# Revit family: Rough_In_Valve-American_Standard-R950-SS
name_source: partatom
category: Plumbing Fixtures
revit_build: Autodesk Revit 2014 (Build: 20130308_1515(x64)
units: mm (PartAtom-declared; Revit-internal decimal feet)

## types (2) — shared parameters
Assembly Code = D2020
CW Connection = Yes
CWFU = 3
Cold Water Connection Diameter = 1/2"
Default Elevation = 0"
HW Connection = Yes
HWFU = 3
Height = 5 5/8"
Hot Water Connection Diameter = 1"
Installation Type = Floor Mounted
Length = 4 9/16"
Manufacturer = American Standard
Material = Copper-American-Standard-000-Brass
Price = Prices may vary. Please consult Manufacturer Representative for most up-to-date price list.
Product Documentation Link = https://www.americanstandard-us.com
Product URL = https://www.americanstandard-us.com
Specification = Free standing tub filler shall feature cast brass construction. Shall also feature integrated dust guard and self- leveling hardware.
URL = https://www.americanstandard-us.com
Vent Connection = No
WFU = 4
Warranty Information = Limited Lifetime Warranty
Waste Connection = No
Width = 4 9/16"

## per-type parameters (varying)
| type | Description | Rough Valve with Service Stops. |
| R950 | R950 FLASH Free Standing Tub Filler Rough Valve. | No |
| R950SS | R950SS FLASH Free Standing Tub Filler Rough Valve with Service Stops. | Yes |

note: column(s) folded — value = type name in every type: Model

## geometry (parser evidence)
native form markers: Sweep x1
no freeform markers — native parametric forms only
